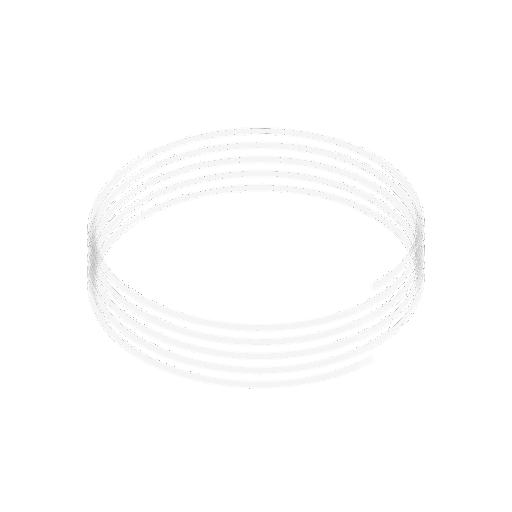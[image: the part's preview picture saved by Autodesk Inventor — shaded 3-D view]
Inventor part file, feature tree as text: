
AUTODESK INVENTOR PART (.ipt)
format: ipt  version: 2024.1 (Build 281209000, 209)  size: 332,800 bytes
history: native  units: mm
features: other x1, sketch x1
ambient origin geometry x8: Origin, YZ Plane, XZ Plane, XY Plane, X Axis, Y Axis, Z Axis, Center Point
bodies: Volumenkörper1 (feature_tree)
feature tree (2):
  other  "Spirale1"
  sketch  "Skizze1"  dims[d0=3.0mm d1=5.0mm d2=10.0mm d3=10.0mm d4=50.0mm d5=0.0mm d6=90.0deg d7=90.0deg d8=0.0mm d9=0.0mm]
